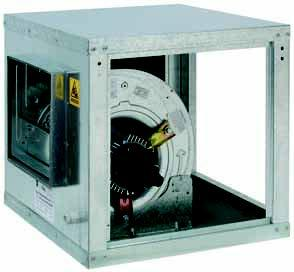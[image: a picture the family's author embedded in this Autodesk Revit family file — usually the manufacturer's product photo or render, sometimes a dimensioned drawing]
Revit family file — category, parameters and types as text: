
# Revit family: BD-ERP_39-39-T6
name_source: partatom
category: Aparatos eléctricos
revit_build: Autodesk Revit 2016 (Build: 20150220_1215(x64)
units: mm (PartAtom-declared; Revit-internal decimal feet)

## family parameters
Compartido = No
Corte con vacíos al cargar = No
Cota de conector redondo = Diámetro de uso
Mantener orientación de anotación = No
Número OmniClass = 23.80.00.00
Punto de cálculo de habitación = No
Se basa en plano de trabajo = No
Siempre vertical = Sí
Tipo de pieza = Caja de conexiones
Título OmniClass = Electric Power and Lighting

## types (1)
- BD ERP
    Caudal máx. = 10700 m3/h
    Clase = F
    Costo = 0 $
    Código de montaje = CV01629
    Descripción = CAJAS DE VENTILACIÓN CON MOTOR INCORPORADO
    Dimensiones exteriores = 720 x 720 x720 mm
    Dimensiones ventana = Ø500 mm
    Fabricante = SALVADOR ESCODA
    Imagen de tipo = CajasVentilacion-BD-ERP.jpg
    Intensidad abs.trifásico. 50Hz-230V = 10,92 A
    Intensidad abs.trifásico. 50Hz-380V = 6,31 A
    Modelo = BD ERP 39/39 T6 CIRCULAR
    Nivel presión sonora = 75 db(A)
    Peso = 80 Kg
    Potencia motor = 2,2 kW
    Protección = IP-55
    URL = www.salvadorescoda.com
    Velocidad = 900 rpm
